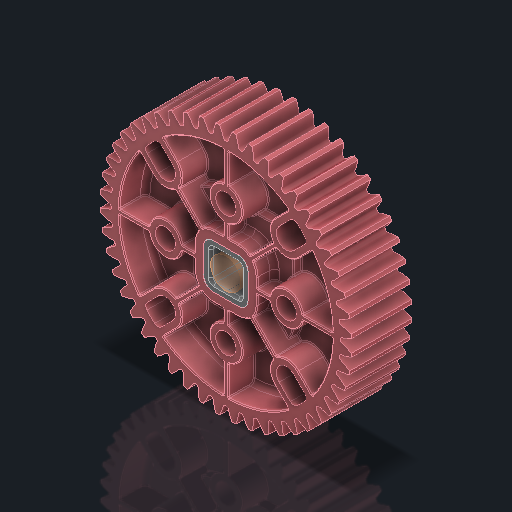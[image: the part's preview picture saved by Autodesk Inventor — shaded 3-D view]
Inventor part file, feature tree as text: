
AUTODESK INVENTOR PART (.ipt)
format: ipt  version: 2023.2 (Build 272271030, 271C)  size: 2,678,272 bytes
history: native  units: in
note: dims shown in document units (in); Inventor stores cm internally (conversion verified against a paired STEP export)
features: other x3, sketch x1, extrude x1
ambient origin geometry x8: Origin, YZ Plane, XZ Plane, XY Plane, X Axis, Y Axis, Z Axis, Center Point
bodies: Solid1 (feature_tree), Solid2 (feature_tree)
feature tree (5):
  sketch  "Sketch1"  dims[d0=0.25in d1=0.3937in d2=0.0in]
  other  "Srf1"
  other  "276-7573-001_OVERMOLD Rev7_48T 24DP Gear_1:1"
  other  "276-7573-002 Rev7_2:1"
  extrude  "ExtrusionSrf1"  Depth=0.3937in TaperAngle=0.0deg
